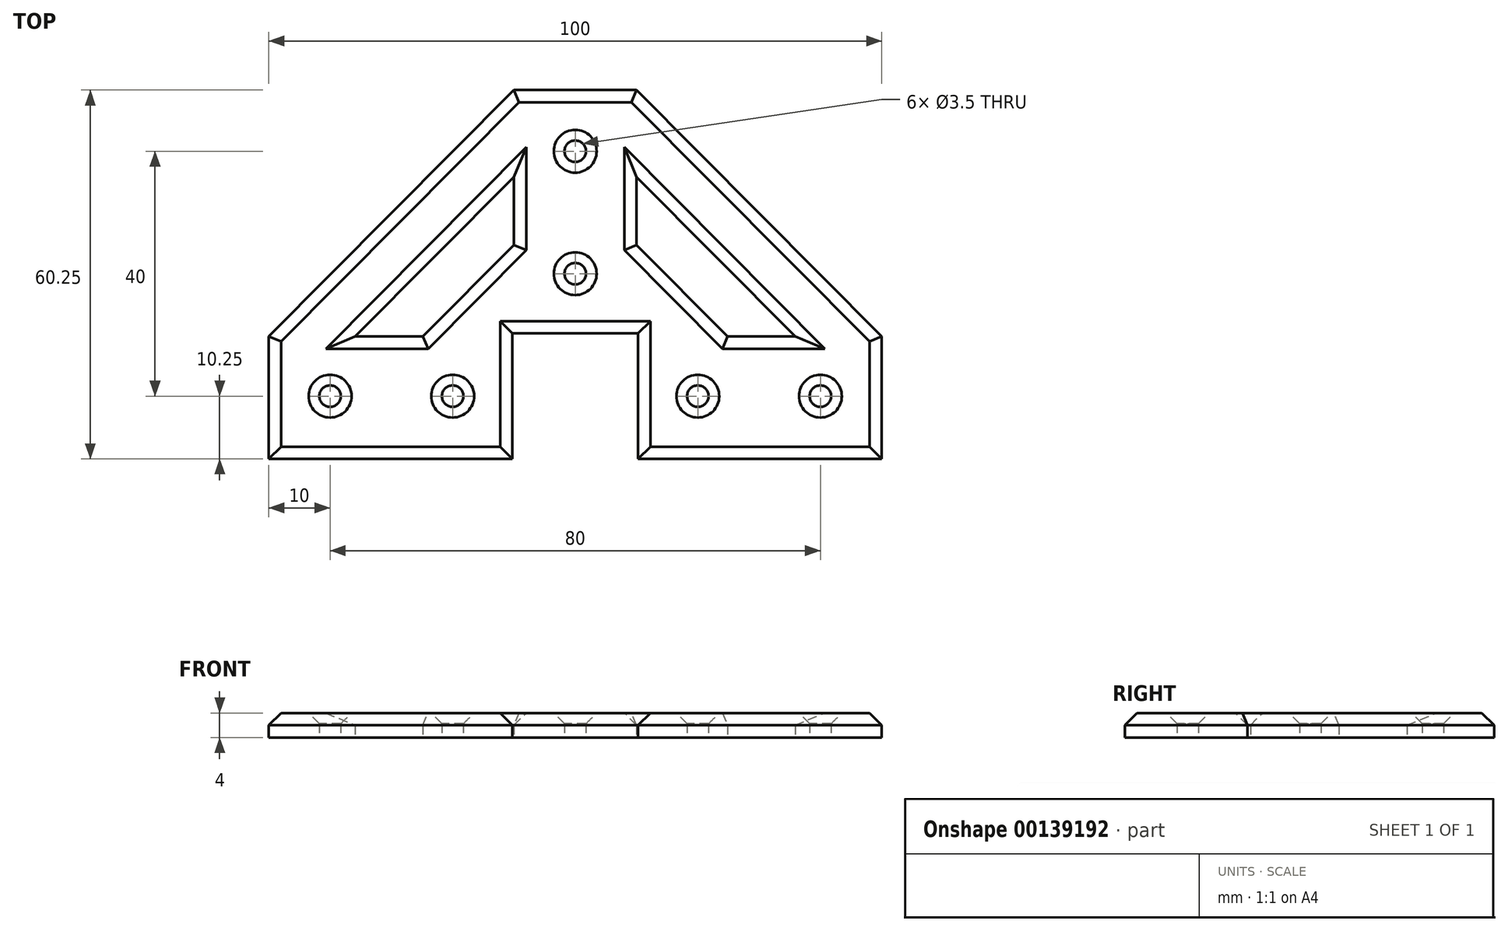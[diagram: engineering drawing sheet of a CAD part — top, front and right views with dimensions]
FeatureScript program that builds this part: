
annotation { "Feature Type Name" : "Feature", "Feature Type Description" : "" }
export const myFeature = defineFeature(function(context is Context, id is Id, definition is map)
    precondition{}
    {
        {
            var Q0;
            Q0=qCreatedBy(makeId("Top.planeOp"),FACE);
            var sketch = newSketch(context, id + "F0", { "sketchPlane" : qUnion([Q0])});
            skLineSegment(sketch, "E0", {"start": v(10.25, -10.25) * mm, "end": v(50, -10.25) * mm});
            skLineSegment(sketch, "E1", {"start": v(50, -10.25) * mm, "end": v(50, 9.75) * mm});
            skLineSegment(sketch, "E2", {"start": v(0, 50) * mm, "end": v(10, 50) * mm});
            skLineSegment(sketch, "E3", {"start": v(10, 50) * mm, "end": v(50, 9.75) * mm});
            skLineSegment(sketch, "E4", {"start": v(10.25, -10.25) * mm, "end": v(10.25, 10.25) * mm});
            skLineSegment(sketch, "E5", {"start": v(10.25, 10.25) * mm, "end": v(0, 10.25) * mm});
            skLineSegment(sketch, "E6", {"start": v(10, 35.81) * mm, "end": v(35.9, 9.75) * mm});
            skLineSegment(sketch, "E7", {"start": v(35.9, 9.75) * mm, "end": v(24.85, 9.75) * mm});
            skLineSegment(sketch, "E8", {"start": v(24.85, 9.75) * mm, "end": v(10, 24.69) * mm});
            skLineSegment(sketch, "E9", {"start": v(10, 24.69) * mm, "end": v(10, 35.81) * mm});
            skCircle(sketch, "E10", {"center": v(20, 0) * mm, "radius": 1.75 * mm});
            skCircle(sketch, "E11", {"center": v(40, 0) * mm, "radius": 1.75 * mm});
            skCircle(sketch, "E12", {"center": v(0, 20) * mm, "radius": 1.75 * mm});
            skCircle(sketch, "E13", {"center": v(0, 40) * mm, "radius": 1.75 * mm});
            skLineSegment(sketch, "E14.MirrorCS", {"start": v(-10.25, -10.25) * mm, "end": v(-50, -10.25) * mm});
            skLineSegment(sketch, "E15.MirrorCS", {"start": v(-50, -10.25) * mm, "end": v(-50, 9.75) * mm});
            skLineSegment(sketch, "E16.MirrorCS", {"start": v(-10, 50) * mm, "end": v(-50, 9.75) * mm});
            skLineSegment(sketch, "E17.MirrorCS", {"start": v(-10.25, -10.25) * mm, "end": v(-10.25, 10.25) * mm});
            skCircle(sketch, "E18.MirrorC", {"center": v(-40, 0) * mm, "radius": 1.75 * mm});
            skLineSegment(sketch, "E19.MirrorCS", {"start": v(-10.25, 10.25) * mm, "end": v(0, 10.25) * mm});
            skLineSegment(sketch, "E20.MirrorCS", {"start": v(-10, 35.81) * mm, "end": v(-35.9, 9.75) * mm});
            skLineSegment(sketch, "E21.MirrorCS", {"start": v(-35.9, 9.75) * mm, "end": v(-24.85, 9.75) * mm});
            skCircle(sketch, "E22.MirrorC", {"center": v(-20, 0) * mm, "radius": 1.75 * mm});
            skLineSegment(sketch, "E23.MirrorCS", {"start": v(0, 50) * mm, "end": v(-10, 50) * mm});
            skLineSegment(sketch, "E24.MirrorCS", {"start": v(-24.85, 9.75) * mm, "end": v(-10, 24.69) * mm});
            skLineSegment(sketch, "E25.MirrorCS", {"start": v(-10, 24.69) * mm, "end": v(-10, 35.81) * mm});
            skSolve(sketch);
        }
        {
            var Q0;
            Q0=makeQuery(id+"F0.imprint","IMPRINT",FACE,{"disambiguationData":[TD([[makeQuery(id+"F0.imprint","IMPRINT",EDGE,{"derivedFrom":sQuery(id+"F0.wireOp",EDGE,"E0")}),1.0]])]});
            extrude(context, id + "F1", {"entities" : qUnion([Q0]), "depth" : 4 * mm});
        }
        {
            var Q0;
            Q0=makeQuery(id+"F1.opExtrude","CAP_EDGE",EDGE,{"disambiguationData":[OSD([sQuery(id+"F0.wireOp",EDGE,"E22.MirrorC")])],"isStart":false});
            var Q1;
            Q1=makeQuery(id+"F1.opExtrude","CAP_EDGE",EDGE,{"disambiguationData":[OSD([sQuery(id+"F0.wireOp",EDGE,"E18.MirrorC")])],"isStart":false});
            var Q2;
            Q2=makeQuery(id+"F1.opExtrude","CAP_EDGE",EDGE,{"disambiguationData":[OSD([sQuery(id+"F0.wireOp",EDGE,"E12")])],"isStart":false});
            var Q3;
            Q3=makeQuery(id+"F1.opExtrude","CAP_EDGE",EDGE,{"disambiguationData":[OSD([sQuery(id+"F0.wireOp",EDGE,"E13")])],"isStart":false});
            var Q4;
            Q4=makeQuery(id+"F1.opExtrude","CAP_EDGE",EDGE,{"disambiguationData":[OSD([sQuery(id+"F0.wireOp",EDGE,"E10")])],"isStart":false});
            var Q5;
            Q5=makeQuery(id+"F1.opExtrude","CAP_EDGE",EDGE,{"disambiguationData":[OSD([sQuery(id+"F0.wireOp",EDGE,"E11")])],"isStart":false});
            chamfer(context, id + "F2", {"entities" : qUnion([Q0, Q1, Q2, Q3, Q4, Q5]), "width" : 1.75 * mm, "tangentPropagation" : true});
        }
        {
            var Q0;
            Q0=makeQuery(id+"F1.opExtrude","CAP_EDGE",EDGE,{"disambiguationData":[OSD([sQuery(id+"F0.wireOp",EDGE,"E16.MirrorCS")])],"isStart":false});
            var Q1;
            Q1=makeQuery(id+"F1.opExtrude","CAP_EDGE",EDGE,{"disambiguationData":[OSD([sQuery(id+"F0.wireOp",EDGE,"E15.MirrorCS")])],"isStart":false});
            var Q2;
            Q2=makeQuery(id+"F1.opExtrude","CAP_EDGE",EDGE,{"disambiguationData":[OSD([sQuery(id+"F0.wireOp",EDGE,"E14.MirrorCS")])],"isStart":false});
            var Q3;
            Q3=makeQuery(id+"F1.opExtrude","CAP_EDGE",EDGE,{"disambiguationData":[OSD([sQuery(id+"F0.wireOp",EDGE,"E17.MirrorCS")])],"isStart":false});
            var Q4;
            Q4=makeQuery(id+"F1.opExtrude","CAP_EDGE",EDGE,{"disambiguationData":[OSD([sQuery(id+"F0.wireOp",EDGE,"E5"),sQuery(id+"F0.wireOp",EDGE,"E19.MirrorCS")])],"isStart":false});
            var Q5;
            Q5=makeQuery(id+"F1.opExtrude","CAP_EDGE",EDGE,{"disambiguationData":[OSD([sQuery(id+"F0.wireOp",EDGE,"E4")])],"isStart":false});
            var Q6;
            Q6=makeQuery(id+"F1.opExtrude","CAP_EDGE",EDGE,{"disambiguationData":[OSD([sQuery(id+"F0.wireOp",EDGE,"E0")])],"isStart":false});
            var Q7;
            Q7=makeQuery(id+"F1.opExtrude","CAP_EDGE",EDGE,{"disambiguationData":[OSD([sQuery(id+"F0.wireOp",EDGE,"E1")])],"isStart":false});
            var Q8;
            Q8=makeQuery(id+"F1.opExtrude","CAP_EDGE",EDGE,{"disambiguationData":[OSD([sQuery(id+"F0.wireOp",EDGE,"E3")])],"isStart":false});
            var Q9;
            Q9=makeQuery(id+"F1.opExtrude","CAP_EDGE",EDGE,{"disambiguationData":[OSD([sQuery(id+"F0.wireOp",EDGE,"E2"),sQuery(id+"F0.wireOp",EDGE,"E23.MirrorCS")])],"isStart":false});
            var Q10;
            Q10=makeQuery(id+"F1.opExtrude","CAP_EDGE",EDGE,{"disambiguationData":[OSD([sQuery(id+"F0.wireOp",EDGE,"E6")])],"isStart":false});
            var Q11;
            Q11=makeQuery(id+"F1.opExtrude","CAP_EDGE",EDGE,{"disambiguationData":[OSD([sQuery(id+"F0.wireOp",EDGE,"E9")])],"isStart":false});
            var Q12;
            Q12=makeQuery(id+"F1.opExtrude","CAP_EDGE",EDGE,{"disambiguationData":[OSD([sQuery(id+"F0.wireOp",EDGE,"E8")])],"isStart":false});
            var Q13;
            Q13=makeQuery(id+"F1.opExtrude","CAP_EDGE",EDGE,{"disambiguationData":[OSD([sQuery(id+"F0.wireOp",EDGE,"E7")])],"isStart":false});
            var Q14;
            Q14=makeQuery(id+"F1.opExtrude","CAP_EDGE",EDGE,{"disambiguationData":[OSD([sQuery(id+"F0.wireOp",EDGE,"E24.MirrorCS")])],"isStart":false});
            var Q15;
            Q15=makeQuery(id+"F1.opExtrude","CAP_EDGE",EDGE,{"disambiguationData":[OSD([sQuery(id+"F0.wireOp",EDGE,"E21.MirrorCS")])],"isStart":false});
            var Q16;
            Q16=makeQuery(id+"F1.opExtrude","CAP_EDGE",EDGE,{"disambiguationData":[OSD([sQuery(id+"F0.wireOp",EDGE,"E20.MirrorCS")])],"isStart":false});
            var Q17;
            Q17=makeQuery(id+"F1.opExtrude","CAP_EDGE",EDGE,{"disambiguationData":[OSD([sQuery(id+"F0.wireOp",EDGE,"E25.MirrorCS")])],"isStart":false});
            chamfer(context, id + "F3", {"entities" : qUnion([Q0, Q1, Q2, Q3, Q4, Q5, Q6, Q7, Q8, Q9, Q10, Q11, Q12, Q13, Q14, Q15, Q16, Q17]), "width" : 2 * mm, "tangentPropagation" : true});
        }
    });
